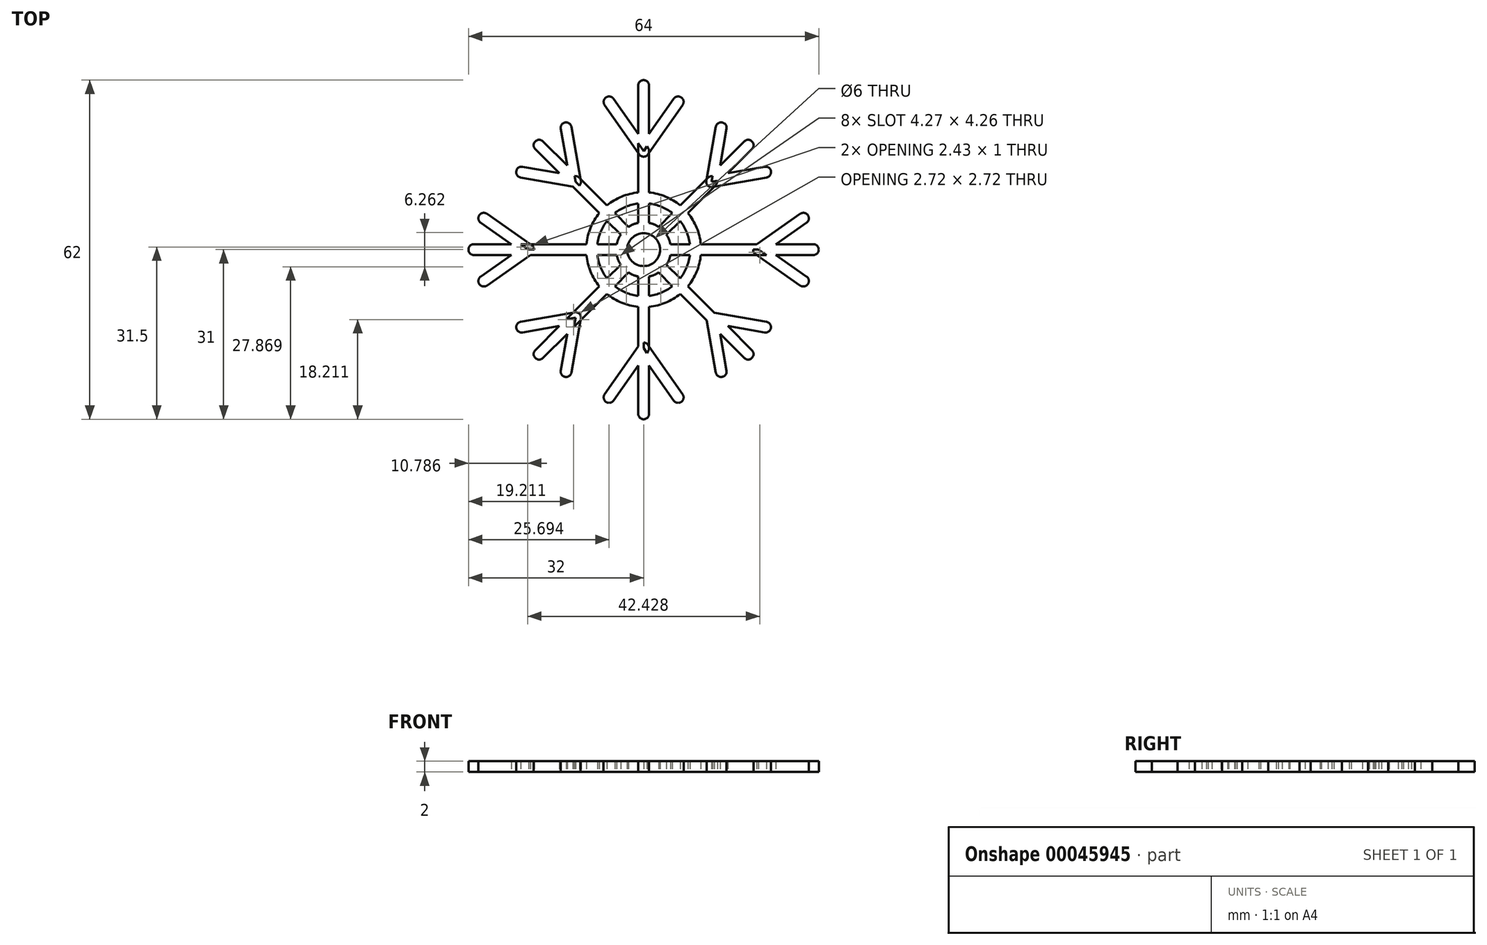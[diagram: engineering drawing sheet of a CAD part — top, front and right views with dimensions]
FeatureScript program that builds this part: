
annotation { "Feature Type Name" : "Feature", "Feature Type Description" : "" }
export const myFeature = defineFeature(function(context is Context, id is Id, definition is map)
    precondition{}
    {
        {
            var Q0;
            Q0=qCreatedBy(makeId("Top.planeOp"),FACE);
            var sketch = newSketch(context, id + "F0", { "sketchPlane" : qUnion([Q0])});
            skLineSegment(sketch, "E0", {"start": v(0, 30) * mm, "end": v(0, -124.41) * mm, "construction": true});
            skLineSegment(sketch, "E1", {"start": v(-154.84, 0) * mm, "end": v(56.08, 0) * mm, "construction": true});
            skCircle(sketch, "E2", {"center": v(0, 0) * mm, "radius": 3 * mm});
            skCircle(sketch, "E3", {"center": v(0, 0) * mm, "radius": 5 * mm});
            skCircle(sketch, "E4", {"center": v(0, 0) * mm, "radius": 8.5 * mm});
            skCircle(sketch, "E5", {"center": v(0, 0) * mm, "radius": 10.5 * mm});
            skLineSegment(sketch, "E6", {"start": v(0, 0) * mm, "end": v(0, 30) * mm});
            skArc(sketch, "E7.0.startCap", {"start": v(1, 0) * mm, "mid": v(0, -1) * mm, "end": v(-1, 0) * mm});
            skArc(sketch, "E7.0.endCap", {"start": v(-1, 30) * mm, "mid": v(0, 31) * mm, "end": v(1, 30) * mm});
            skLineSegment(sketch, "E7.0.left", {"start": v(-1, 0) * mm, "end": v(-1, 30) * mm});
            skLineSegment(sketch, "E7.0.right", {"start": v(1, 0) * mm, "end": v(1, 30) * mm});
            skLineSegment(sketch, "E8", {"start": v(1, 0) * mm, "end": v(31, 0) * mm});
            skArc(sketch, "E9.0.startCap", {"start": v(1, -1) * mm, "mid": v(0, 0) * mm, "end": v(1, 1) * mm});
            skArc(sketch, "E9.0.endCap", {"start": v(31, 1) * mm, "mid": v(32, 0) * mm, "end": v(31, -1) * mm});
            skLineSegment(sketch, "E9.0.left", {"start": v(1, 1) * mm, "end": v(31, 1) * mm});
            skLineSegment(sketch, "E9.0.right", {"start": v(1, -1) * mm, "end": v(31, -1) * mm});
            skLineSegment(sketch, "E10", {"start": v(0, 18) * mm, "end": v(6.3, 27.01) * mm});
            skArc(sketch, "E11.0.startCap", {"start": v(0.82, 17.43) * mm, "mid": v(-0.57, 17.18) * mm, "end": v(-0.82, 18.57) * mm});
            skArc(sketch, "E11.0.endCap", {"start": v(5.5, 27.58) * mm, "mid": v(6.88, 27.83) * mm, "end": v(7.13, 26.44) * mm});
            skLineSegment(sketch, "E11.0.left", {"start": v(-0.82, 18.57) * mm, "end": v(5.5, 27.58) * mm});
            skLineSegment(sketch, "E11.0.right", {"start": v(0.82, 17.43) * mm, "end": v(7.13, 26.44) * mm});
            skLineSegment(sketch, "E12", {"start": v(0, 0) * mm, "end": v(19.1, 19.1) * mm});
            skArc(sketch, "E13.0.startCap", {"start": v(0.7, -0.7) * mm, "mid": v(-0.7, -0.7) * mm, "end": v(-0.7, 0.7) * mm});
            skArc(sketch, "E13.0.endCap", {"start": v(18.38, 19.8) * mm, "mid": v(19.8, 19.8) * mm, "end": v(19.8, 18.38) * mm});
            skLineSegment(sketch, "E13.0.left", {"start": v(-0.7, 0.7) * mm, "end": v(18.38, 19.8) * mm});
            skLineSegment(sketch, "E13.0.right", {"start": v(0.7, -0.7) * mm, "end": v(19.8, 18.38) * mm});
            skLineSegment(sketch, "E14", {"start": v(21, 0) * mm, "end": v(29.2, 5.74) * mm});
            skArc(sketch, "E15.0.startCap", {"start": v(21.57, -0.82) * mm, "mid": v(20.18, -0.57) * mm, "end": v(20.43, 0.82) * mm});
            skArc(sketch, "E15.0.endCap", {"start": v(28.62, 6.55) * mm, "mid": v(30.01, 6.3) * mm, "end": v(29.77, 4.92) * mm});
            skLineSegment(sketch, "E15.0.left", {"start": v(20.43, 0.82) * mm, "end": v(28.62, 6.55) * mm});
            skLineSegment(sketch, "E15.0.right", {"start": v(21.57, -0.82) * mm, "end": v(29.77, 4.92) * mm});
            skLineSegment(sketch, "E16", {"start": v(12.43, 12.43) * mm, "end": v(22.28, 14.17) * mm});
            skLineSegment(sketch, "E17", {"start": v(12.43, 12.43) * mm, "end": v(14.17, 22.28) * mm});
            skArc(sketch, "E18.0.startCap", {"start": v(13.42, 12.26) * mm, "mid": v(12.26, 11.45) * mm, "end": v(11.45, 12.6) * mm});
            skArc(sketch, "E18.0.endCap", {"start": v(13.18, 22.45) * mm, "mid": v(14.34, 23.26) * mm, "end": v(15.15, 22.1) * mm});
            skLineSegment(sketch, "E18.0.left", {"start": v(11.45, 12.6) * mm, "end": v(13.18, 22.45) * mm});
            skLineSegment(sketch, "E18.0.right", {"start": v(13.42, 12.26) * mm, "end": v(15.15, 22.1) * mm});
            skArc(sketch, "E18.1.startCap", {"start": v(12.6, 11.45) * mm, "mid": v(11.45, 12.26) * mm, "end": v(12.26, 13.42) * mm});
            skArc(sketch, "E18.1.endCap", {"start": v(22.1, 15.15) * mm, "mid": v(23.26, 14.34) * mm, "end": v(22.45, 13.18) * mm});
            skLineSegment(sketch, "E18.1.left", {"start": v(12.26, 13.42) * mm, "end": v(22.1, 15.15) * mm});
            skLineSegment(sketch, "E18.1.right", {"start": v(12.6, 11.45) * mm, "end": v(22.45, 13.18) * mm});
            skArc(sketch, "E19.MirrorCS", {"start": v(0.7, 0.7) * mm, "mid": v(-0.7, 0.7) * mm, "end": v(-0.7, -0.7) * mm});
            skArc(sketch, "E20.MirrorCS", {"start": v(1, 0) * mm, "mid": v(0, 1) * mm, "end": v(-1, 0) * mm});
            skArc(sketch, "E21.MirrorCS", {"start": v(1, 1) * mm, "mid": v(0, 0) * mm, "end": v(1, -1) * mm});
            skArc(sketch, "E22.MirrorCS", {"start": v(12.6, -11.45) * mm, "mid": v(11.45, -12.26) * mm, "end": v(12.26, -13.42) * mm});
            skArc(sketch, "E23.MirrorCS", {"start": v(-1, -30) * mm, "mid": v(0, -31) * mm, "end": v(1, -30) * mm});
            skArc(sketch, "E24.MirrorCS", {"start": v(13.42, -12.26) * mm, "mid": v(12.26, -11.45) * mm, "end": v(11.45, -12.6) * mm});
            skArc(sketch, "E25.MirrorCS", {"start": v(21.57, 0.82) * mm, "mid": v(20.18, 0.57) * mm, "end": v(20.43, -0.82) * mm});
            skArc(sketch, "E26.MirrorCS", {"start": v(13.18, -22.45) * mm, "mid": v(14.34, -23.26) * mm, "end": v(15.15, -22.1) * mm});
            skArc(sketch, "E27.MirrorCS", {"start": v(28.62, -6.55) * mm, "mid": v(30.01, -6.3) * mm, "end": v(29.77, -4.92) * mm});
            skArc(sketch, "E28.MirrorCS", {"start": v(5.5, -27.58) * mm, "mid": v(6.88, -27.83) * mm, "end": v(7.13, -26.44) * mm});
            skArc(sketch, "E29.MirrorCS", {"start": v(18.38, -19.8) * mm, "mid": v(19.8, -19.8) * mm, "end": v(19.8, -18.38) * mm});
            skArc(sketch, "E30.MirrorCS", {"start": v(22.1, -15.15) * mm, "mid": v(23.26, -14.34) * mm, "end": v(22.45, -13.18) * mm});
            skArc(sketch, "E31.MirrorCS", {"start": v(31, -1) * mm, "mid": v(32, 0) * mm, "end": v(31, 1) * mm});
            skArc(sketch, "E32.MirrorCS", {"start": v(0.82, -17.43) * mm, "mid": v(-0.57, -17.18) * mm, "end": v(-0.82, -18.57) * mm});
            skLineSegment(sketch, "E33.MirrorCS", {"start": v(11.45, -12.6) * mm, "end": v(13.18, -22.45) * mm});
            skLineSegment(sketch, "E34.MirrorCS", {"start": v(21, 0) * mm, "end": v(29.2, -5.74) * mm});
            skLineSegment(sketch, "E35.MirrorCS", {"start": v(-0.82, -18.57) * mm, "end": v(5.5, -27.58) * mm});
            skLineSegment(sketch, "E36.MirrorCS", {"start": v(0.82, -17.43) * mm, "end": v(7.13, -26.44) * mm});
            skLineSegment(sketch, "E37.MirrorCS", {"start": v(13.42, -12.26) * mm, "end": v(15.15, -22.1) * mm});
            skLineSegment(sketch, "E38.MirrorCS", {"start": v(20.43, -0.82) * mm, "end": v(28.62, -6.55) * mm});
            skLineSegment(sketch, "E39.MirrorCS", {"start": v(0, 0) * mm, "end": v(19.1, -19.1) * mm});
            skLineSegment(sketch, "E40.MirrorCS", {"start": v(21.57, 0.82) * mm, "end": v(29.77, -4.92) * mm});
            skLineSegment(sketch, "E41.MirrorCS", {"start": v(0, 0) * mm, "end": v(0, -30) * mm});
            skLineSegment(sketch, "E42.MirrorCS", {"start": v(-1, 0) * mm, "end": v(-1, -30) * mm});
            skLineSegment(sketch, "E43.MirrorCS", {"start": v(1, 0) * mm, "end": v(1, -30) * mm});
            skLineSegment(sketch, "E44.MirrorCS", {"start": v(0.7, 0.7) * mm, "end": v(19.8, -18.38) * mm});
            skLineSegment(sketch, "E45.MirrorCS", {"start": v(12.26, -13.42) * mm, "end": v(22.1, -15.15) * mm});
            skLineSegment(sketch, "E46.MirrorCS", {"start": v(0, -18) * mm, "end": v(6.3, -27.01) * mm});
            skLineSegment(sketch, "E47.MirrorCS", {"start": v(12.43, -12.43) * mm, "end": v(14.17, -22.28) * mm});
            skLineSegment(sketch, "E48.MirrorCS", {"start": v(12.43, -12.43) * mm, "end": v(22.28, -14.17) * mm});
            skLineSegment(sketch, "E49.MirrorCS", {"start": v(12.6, -11.45) * mm, "end": v(22.45, -13.18) * mm});
            skLineSegment(sketch, "E50.MirrorCS", {"start": v(-0.7, -0.7) * mm, "end": v(18.38, -19.8) * mm});
            skArc(sketch, "E51.MirrorCS", {"start": v(-0.7, -0.7) * mm, "mid": v(0.7, -0.7) * mm, "end": v(0.7, 0.7) * mm});
            skArc(sketch, "E52.MirrorCS", {"start": v(-1, 1) * mm, "mid": v(0, 0) * mm, "end": v(-1, -1) * mm});
            skArc(sketch, "E53.MirrorCS", {"start": v(-0.7, 0.7) * mm, "mid": v(0.7, 0.7) * mm, "end": v(0.7, -0.7) * mm});
            skArc(sketch, "E54.MirrorCS", {"start": v(-1, -1) * mm, "mid": v(0, 0) * mm, "end": v(-1, 1) * mm});
            skArc(sketch, "E55.MirrorCS", {"start": v(-1, 0) * mm, "mid": v(0, -1) * mm, "end": v(1, 0) * mm});
            skArc(sketch, "E56.MirrorCS", {"start": v(-1, 0) * mm, "mid": v(0, 1) * mm, "end": v(1, 0) * mm});
            skArc(sketch, "E57.MirrorCS", {"start": v(-13.42, -12.26) * mm, "mid": v(-12.26, -11.45) * mm, "end": v(-11.45, -12.6) * mm});
            skArc(sketch, "E58.MirrorCS", {"start": v(-12.6, -11.45) * mm, "mid": v(-11.45, -12.26) * mm, "end": v(-12.26, -13.42) * mm});
            skArc(sketch, "E59.MirrorCS", {"start": v(-31, -1) * mm, "mid": v(-32, 0) * mm, "end": v(-31, 1) * mm});
            skArc(sketch, "E60.MirrorCS", {"start": v(-13.42, 12.26) * mm, "mid": v(-12.26, 11.45) * mm, "end": v(-11.45, 12.6) * mm});
            skArc(sketch, "E61.MirrorCS", {"start": v(-31, 1) * mm, "mid": v(-32, 0) * mm, "end": v(-31, -1) * mm});
            skArc(sketch, "E62.MirrorCS", {"start": v(-12.6, 11.45) * mm, "mid": v(-11.45, 12.26) * mm, "end": v(-12.26, 13.42) * mm});
            skArc(sketch, "E63.MirrorCS", {"start": v(1, 30) * mm, "mid": v(0, 31) * mm, "end": v(-1, 30) * mm});
            skArc(sketch, "E64.MirrorCS", {"start": v(-21.57, 0.82) * mm, "mid": v(-20.18, 0.57) * mm, "end": v(-20.43, -0.82) * mm});
            skArc(sketch, "E65.MirrorCS", {"start": v(-21.57, -0.82) * mm, "mid": v(-20.18, -0.57) * mm, "end": v(-20.43, 0.82) * mm});
            skArc(sketch, "E66.MirrorCS", {"start": v(-13.18, 22.45) * mm, "mid": v(-14.34, 23.26) * mm, "end": v(-15.15, 22.1) * mm});
            skArc(sketch, "E67.MirrorCS", {"start": v(-13.18, -22.45) * mm, "mid": v(-14.34, -23.26) * mm, "end": v(-15.15, -22.1) * mm});
            skArc(sketch, "E68.MirrorCS", {"start": v(1, -30) * mm, "mid": v(0, -31) * mm, "end": v(-1, -30) * mm});
            skArc(sketch, "E69.MirrorCS", {"start": v(-22.1, -15.15) * mm, "mid": v(-23.26, -14.34) * mm, "end": v(-22.45, -13.18) * mm});
            skArc(sketch, "E70.MirrorCS", {"start": v(-5.5, -27.58) * mm, "mid": v(-6.88, -27.83) * mm, "end": v(-7.13, -26.44) * mm});
            skArc(sketch, "E71.MirrorCS", {"start": v(-5.5, 27.58) * mm, "mid": v(-6.88, 27.83) * mm, "end": v(-7.13, 26.44) * mm});
            skArc(sketch, "E72.MirrorCS", {"start": v(-28.62, -6.55) * mm, "mid": v(-30.01, -6.3) * mm, "end": v(-29.77, -4.92) * mm});
            skArc(sketch, "E73.MirrorCS", {"start": v(-0.82, 17.43) * mm, "mid": v(0.57, 17.18) * mm, "end": v(0.82, 18.57) * mm});
            skArc(sketch, "E74.MirrorCS", {"start": v(-28.62, 6.55) * mm, "mid": v(-30.01, 6.3) * mm, "end": v(-29.77, 4.92) * mm});
            skArc(sketch, "E75.MirrorCS", {"start": v(-18.38, 19.8) * mm, "mid": v(-19.8, 19.8) * mm, "end": v(-19.8, 18.38) * mm});
            skArc(sketch, "E76.MirrorCS", {"start": v(-22.1, 15.15) * mm, "mid": v(-23.26, 14.34) * mm, "end": v(-22.45, 13.18) * mm});
            skArc(sketch, "E77.MirrorCS", {"start": v(-0.82, -17.43) * mm, "mid": v(0.57, -17.18) * mm, "end": v(0.82, -18.57) * mm});
            skArc(sketch, "E78.MirrorCS", {"start": v(-18.38, -19.8) * mm, "mid": v(-19.8, -19.8) * mm, "end": v(-19.8, -18.38) * mm});
            skLineSegment(sketch, "E79.MirrorCS", {"start": v(-1, 0) * mm, "end": v(-31, 0) * mm});
            skLineSegment(sketch, "E80.MirrorCS", {"start": v(-1, 1) * mm, "end": v(-31, 1) * mm});
            skLineSegment(sketch, "E81.MirrorCS", {"start": v(-1, -1) * mm, "end": v(-31, -1) * mm});
            skLineSegment(sketch, "E82.MirrorCS", {"start": v(-11.45, 12.6) * mm, "end": v(-13.18, 22.45) * mm});
            skLineSegment(sketch, "E83.MirrorCS", {"start": v(-12.43, 12.43) * mm, "end": v(-14.17, 22.28) * mm});
            skLineSegment(sketch, "E84.MirrorCS", {"start": v(0, 18) * mm, "end": v(-6.3, 27.01) * mm});
            skLineSegment(sketch, "E85.MirrorCS", {"start": v(-12.43, 12.43) * mm, "end": v(-22.28, 14.17) * mm});
            skLineSegment(sketch, "E86.MirrorCS", {"start": v(-21.57, -0.82) * mm, "end": v(-29.77, 4.92) * mm});
            skLineSegment(sketch, "E87.MirrorCS", {"start": v(-21.57, 0.82) * mm, "end": v(-29.77, -4.92) * mm});
            skLineSegment(sketch, "E88.MirrorCS", {"start": v(-20.43, -0.82) * mm, "end": v(-28.62, -6.55) * mm});
            skLineSegment(sketch, "E89.MirrorCS", {"start": v(-20.43, 0.82) * mm, "end": v(-28.62, 6.55) * mm});
            skLineSegment(sketch, "E90.MirrorCS", {"start": v(0, 0) * mm, "end": v(-19.1, -19.1) * mm});
            skLineSegment(sketch, "E91.MirrorCS", {"start": v(-12.6, -11.45) * mm, "end": v(-22.45, -13.18) * mm});
            skLineSegment(sketch, "E92.MirrorCS", {"start": v(0.7, 0.7) * mm, "end": v(-18.38, 19.8) * mm});
            skLineSegment(sketch, "E93.MirrorCS", {"start": v(-12.6, 11.45) * mm, "end": v(-22.45, 13.18) * mm});
            skLineSegment(sketch, "E94.MirrorCS", {"start": v(-13.42, -12.26) * mm, "end": v(-15.15, -22.1) * mm});
            skLineSegment(sketch, "E95.MirrorCS", {"start": v(-21, 0) * mm, "end": v(-29.2, -5.74) * mm});
            skLineSegment(sketch, "E96.MirrorCS", {"start": v(-12.43, -12.43) * mm, "end": v(-22.28, -14.17) * mm});
            skLineSegment(sketch, "E97.MirrorCS", {"start": v(-12.26, 13.42) * mm, "end": v(-22.1, 15.15) * mm});
            skLineSegment(sketch, "E98.MirrorCS", {"start": v(-11.45, -12.6) * mm, "end": v(-13.18, -22.45) * mm});
            skLineSegment(sketch, "E99.MirrorCS", {"start": v(-21, 0) * mm, "end": v(-29.2, 5.74) * mm});
            skLineSegment(sketch, "E100.MirrorCS", {"start": v(-12.43, -12.43) * mm, "end": v(-14.17, -22.28) * mm});
            skLineSegment(sketch, "E101.MirrorCS", {"start": v(-0.82, -17.43) * mm, "end": v(-7.13, -26.44) * mm});
            skLineSegment(sketch, "E102.MirrorCS", {"start": v(-13.42, 12.26) * mm, "end": v(-15.15, 22.1) * mm});
            skLineSegment(sketch, "E103.MirrorCS", {"start": v(-12.26, -13.42) * mm, "end": v(-22.1, -15.15) * mm});
            skLineSegment(sketch, "E104.MirrorCS", {"start": v(-0.82, 17.43) * mm, "end": v(-7.13, 26.44) * mm});
            skLineSegment(sketch, "E105.MirrorCS", {"start": v(0.82, 18.57) * mm, "end": v(-5.5, 27.58) * mm});
            skLineSegment(sketch, "E106.MirrorCS", {"start": v(0, 0) * mm, "end": v(-19.1, 19.1) * mm});
            skLineSegment(sketch, "E107.MirrorCS", {"start": v(-0.7, -0.7) * mm, "end": v(-19.8, 18.38) * mm});
            skLineSegment(sketch, "E108.MirrorCS", {"start": v(0.7, -0.7) * mm, "end": v(-18.38, -19.8) * mm});
            skLineSegment(sketch, "E109.MirrorCS", {"start": v(0.82, -18.57) * mm, "end": v(-5.5, -27.58) * mm});
            skLineSegment(sketch, "E110.MirrorCS", {"start": v(-0.7, 0.7) * mm, "end": v(-19.8, -18.38) * mm});
            skLineSegment(sketch, "E111.MirrorCS", {"start": v(0, -18) * mm, "end": v(-6.3, -27.01) * mm});
            skSolve(sketch);
        }
        {
            var Q0;
            Q0 = qSketchRegion(id + "F0", true);
            var Q1;
            {var subQ1=sQuery(id+"F0.wireOp",EDGE,"E62.MirrorCS");var subQ8=makeQuery(id+"F0.imprint","INTERSECT",VERTEX,{"derivedFrom":[subQ1,sQuery(id+"F0.wireOp",EDGE,"E82.MirrorCS")]});Q1=makeQuery(id+"F0.imprint","IMPRINT",FACE,{"disambiguationData":[TD([[makeQuery(id+"F0.imprint","IMPRINT",EDGE,{"disambiguationData":[TD([[subQ8,1.0]])],"derivedFrom":subQ1}),1.0]])]});}
            var Q2;
            {var subQ1=sQuery(id+"F0.wireOp",EDGE,"E97.MirrorCS");var subQ3=sQuery(id+"F0.wireOp",EDGE,"E83.MirrorCS");var subQ5=makeQuery(id+"F0.imprint","INTERSECT",VERTEX,{"derivedFrom":[subQ3,subQ1]});Q2=makeQuery(id+"F0.imprint","IMPRINT",FACE,{"disambiguationData":[TD([[makeQuery(id+"F0.imprint","IMPRINT",EDGE,{"disambiguationData":[TD([[subQ5,1.0]])],"derivedFrom":subQ3}),1.0]])]});}
            var Q3;
            {var subQ1=sQuery(id+"F0.wireOp",EDGE,"E97.MirrorCS");var subQ5=sQuery(id+"F0.wireOp",EDGE,"E62.MirrorCS");var subQ6=makeQuery(id+"F0.imprint","INTERSECT",VERTEX,{"derivedFrom":[subQ5,subQ1]});Q3=makeQuery(id+"F0.imprint","IMPRINT",FACE,{"disambiguationData":[TD([[makeQuery(id+"F0.imprint","IMPRINT",EDGE,{"disambiguationData":[TD([[subQ6,1.0]])],"derivedFrom":subQ5}),-1.0]])]});}
            var Q4;
            {var subQ1=sQuery(id+"F0.wireOp",EDGE,"E102.MirrorCS");var subQ3=sQuery(id+"F0.wireOp",EDGE,"E85.MirrorCS");var subQ5=makeQuery(id+"F0.imprint","INTERSECT",VERTEX,{"derivedFrom":[subQ3,subQ1]});Q4=makeQuery(id+"F0.imprint","IMPRINT",FACE,{"disambiguationData":[TD([[makeQuery(id+"F0.imprint","IMPRINT",EDGE,{"disambiguationData":[TD([[subQ5,1.0]])],"derivedFrom":subQ3}),-1.0]])]});}
            var Q5;
            {var subQ1=sQuery(id+"F0.wireOp",EDGE,"E60.MirrorCS");var subQ5=sQuery(id+"F0.wireOp",EDGE,"E102.MirrorCS");var subQ7=makeQuery(id+"F0.imprint","INTERSECT",VERTEX,{"derivedFrom":[subQ1,subQ5]});Q5=makeQuery(id+"F0.imprint","IMPRINT",FACE,{"disambiguationData":[TD([[makeQuery(id+"F0.imprint","IMPRINT",EDGE,{"disambiguationData":[TD([[subQ7,-1.0]])],"derivedFrom":subQ1}),-1.0]])]});}
            var Q6;
            {var subQ5=sQuery(id+"F0.wireOp",EDGE,"E102.MirrorCS");var subQ7=sQuery(id+"F0.wireOp",EDGE,"E60.MirrorCS");var subQ8=makeQuery(id+"F0.imprint","INTERSECT",VERTEX,{"derivedFrom":[subQ7,subQ5]});Q6=makeQuery(id+"F0.imprint","IMPRINT",FACE,{"disambiguationData":[TD([[makeQuery(id+"F0.imprint","IMPRINT",EDGE,{"disambiguationData":[TD([[subQ8,-1.0]])],"derivedFrom":subQ7}),1.0]])]});}
            var Q7;
            {var subQ5=sQuery(id+"F0.wireOp",EDGE,"E11.0.left");var subQ7=sQuery(id+"F0.wireOp",EDGE,"E11.0.startCap");var subQ10=makeQuery(id+"F0.imprint","INTERSECT",VERTEX,{"derivedFrom":[subQ7,subQ5]});Q7=makeQuery(id+"F0.imprint","IMPRINT",FACE,{"disambiguationData":[TD([[makeQuery(id+"F0.imprint","IMPRINT",EDGE,{"disambiguationData":[TD([[subQ10,1.0]])],"derivedFrom":subQ7}),-1.0]])]});}
            var Q8;
            {var subQ1=sQuery(id+"F0.wireOp",EDGE,"E11.0.startCap");var subQ5=sQuery(id+"F0.wireOp",EDGE,"E11.0.left");var subQ7=makeQuery(id+"F0.imprint","INTERSECT",VERTEX,{"derivedFrom":[subQ1,subQ5]});Q8=makeQuery(id+"F0.imprint","IMPRINT",FACE,{"disambiguationData":[TD([[makeQuery(id+"F0.imprint","IMPRINT",EDGE,{"disambiguationData":[TD([[subQ7,1.0]])],"derivedFrom":subQ1}),1.0]])]});}
            var Q9;
            {var subQ0=sQuery(id+"F0.wireOp",EDGE,"E84.MirrorCS");var subQ1=sQuery(id+"F0.wireOp",EDGE,"E11.0.left");var subQ2=makeQuery(id+"F0.imprint","INTERSECT",VERTEX,{"derivedFrom":[subQ1,subQ0]});Q9=makeQuery(id+"F0.imprint","IMPRINT",FACE,{"disambiguationData":[TD([[makeQuery(id+"F0.imprint","IMPRINT",EDGE,{"disambiguationData":[TD([[subQ2,-1.0]])],"derivedFrom":subQ1}),-1.0]])]});}
            var Q10;
            {var subQ0=sQuery(id+"F0.wireOp",EDGE,"E105.MirrorCS");var subQ3=sQuery(id+"F0.wireOp",EDGE,"E10");var subQ4=makeQuery(id+"F0.imprint","INTERSECT",VERTEX,{"derivedFrom":[subQ3,subQ0]});Q10=makeQuery(id+"F0.imprint","IMPRINT",FACE,{"disambiguationData":[TD([[makeQuery(id+"F0.imprint","IMPRINT",EDGE,{"disambiguationData":[TD([[subQ4,1.0]])],"derivedFrom":subQ3}),1.0]])]});}
            var Q11;
            {var subQ3=sQuery(id+"F0.wireOp",EDGE,"E73.MirrorCS");var subQ8=makeQuery(id+"F0.imprint","INTERSECT",VERTEX,{"derivedFrom":[sQuery(id+"F0.wireOp",EDGE,"E11.0.right"),subQ3]});Q11=makeQuery(id+"F0.imprint","IMPRINT",FACE,{"disambiguationData":[TD([[makeQuery(id+"F0.imprint","IMPRINT",EDGE,{"disambiguationData":[TD([[subQ8,1.0]])],"derivedFrom":subQ3}),1.0]])]});}
            var Q12;
            {var subQ1=sQuery(id+"F0.wireOp",EDGE,"E7.0.right");var subQ5=sQuery(id+"F0.wireOp",EDGE,"E10");var subQ7=makeQuery(id+"F0.imprint","INTERSECT",VERTEX,{"derivedFrom":[subQ5,subQ1]});Q12=makeQuery(id+"F0.imprint","IMPRINT",FACE,{"disambiguationData":[TD([[makeQuery(id+"F0.imprint","IMPRINT",EDGE,{"disambiguationData":[TD([[subQ7,1.0]])],"derivedFrom":subQ5}),-1.0]])]});}
            var Q13;
            {var subQ0=sQuery(id+"F0.wireOp",EDGE,"E18.1.left");var subQ3=sQuery(id+"F0.wireOp",EDGE,"E17");var subQ4=makeQuery(id+"F0.imprint","INTERSECT",VERTEX,{"derivedFrom":[subQ3,subQ0]});Q13=makeQuery(id+"F0.imprint","IMPRINT",FACE,{"disambiguationData":[TD([[makeQuery(id+"F0.imprint","IMPRINT",EDGE,{"disambiguationData":[TD([[subQ4,1.0]])],"derivedFrom":subQ3}),-1.0]])]});}
            var Q14;
            {var subQ0=sQuery(id+"F0.wireOp",EDGE,"E16");var subQ1=sQuery(id+"F0.wireOp",EDGE,"E18.0.right");var subQ2=makeQuery(id+"F0.imprint","INTERSECT",VERTEX,{"derivedFrom":[subQ0,subQ1]});Q14=makeQuery(id+"F0.imprint","IMPRINT",FACE,{"disambiguationData":[TD([[makeQuery(id+"F0.imprint","IMPRINT",EDGE,{"disambiguationData":[TD([[subQ2,1.0]])],"derivedFrom":subQ0}),1.0]])]});}
            var Q15;
            {var subQ0=sQuery(id+"F0.wireOp",EDGE,"E18.1.startCap");var subQ9=makeQuery(id+"F0.imprint","INTERSECT",VERTEX,{"derivedFrom":[sQuery(id+"F0.wireOp",EDGE,"E18.0.left"),subQ0]});Q15=makeQuery(id+"F0.imprint","IMPRINT",FACE,{"disambiguationData":[TD([[makeQuery(id+"F0.imprint","IMPRINT",EDGE,{"disambiguationData":[TD([[subQ9,1.0]])],"derivedFrom":subQ0}),-1.0]])]});}
            var Q16;
            {var subQ1=sQuery(id+"F0.wireOp",EDGE,"E17");var subQ5=sQuery(id+"F0.wireOp",EDGE,"E13.0.left");var subQ7=makeQuery(id+"F0.imprint","INTERSECT",VERTEX,{"derivedFrom":[subQ5,subQ1]});Q16=makeQuery(id+"F0.imprint","IMPRINT",FACE,{"disambiguationData":[TD([[makeQuery(id+"F0.imprint","IMPRINT",EDGE,{"disambiguationData":[TD([[subQ7,1.0]])],"derivedFrom":subQ5}),-1.0]])]});}
            var Q17;
            {var subQ5=sQuery(id+"F0.wireOp",EDGE,"E18.0.startCap");var subQ7=sQuery(id+"F0.wireOp",EDGE,"E18.0.right");var subQ10=makeQuery(id+"F0.imprint","INTERSECT",VERTEX,{"derivedFrom":[subQ5,subQ7]});Q17=makeQuery(id+"F0.imprint","IMPRINT",FACE,{"disambiguationData":[TD([[makeQuery(id+"F0.imprint","IMPRINT",EDGE,{"disambiguationData":[TD([[subQ10,-1.0]])],"derivedFrom":subQ5}),-1.0]])]});}
            var Q18;
            {var subQ1=sQuery(id+"F0.wireOp",EDGE,"E16");var subQ5=sQuery(id+"F0.wireOp",EDGE,"E13.0.right");var subQ7=makeQuery(id+"F0.imprint","INTERSECT",VERTEX,{"derivedFrom":[subQ5,subQ1]});Q18=makeQuery(id+"F0.imprint","IMPRINT",FACE,{"disambiguationData":[TD([[makeQuery(id+"F0.imprint","IMPRINT",EDGE,{"disambiguationData":[TD([[subQ7,1.0]])],"derivedFrom":subQ5}),1.0]])]});}
            var Q19;
            {var subQ0=sQuery(id+"F0.wireOp",EDGE,"E9.0.left");var subQ3=sQuery(id+"F0.wireOp",EDGE,"E14");var subQ4=makeQuery(id+"F0.imprint","INTERSECT",VERTEX,{"derivedFrom":[subQ3,subQ0]});Q19=makeQuery(id+"F0.imprint","IMPRINT",FACE,{"disambiguationData":[TD([[makeQuery(id+"F0.imprint","IMPRINT",EDGE,{"disambiguationData":[TD([[subQ4,1.0]])],"derivedFrom":subQ3}),1.0]])]});}
            var Q20;
            {var subQ1=sQuery(id+"F0.wireOp",EDGE,"E25.MirrorCS");var subQ5=sQuery(id+"F0.wireOp",EDGE,"E40.MirrorCS");var subQ7=makeQuery(id+"F0.imprint","INTERSECT",VERTEX,{"derivedFrom":[subQ1,subQ5]});Q20=makeQuery(id+"F0.imprint","IMPRINT",FACE,{"disambiguationData":[TD([[makeQuery(id+"F0.imprint","IMPRINT",EDGE,{"disambiguationData":[TD([[subQ7,-1.0]])],"derivedFrom":subQ1}),1.0]])]});}
            var Q21;
            {var subQ1=sQuery(id+"F0.wireOp",EDGE,"E40.MirrorCS");var subQ3=sQuery(id+"F0.wireOp",EDGE,"E14");var subQ5=makeQuery(id+"F0.imprint","INTERSECT",VERTEX,{"derivedFrom":[subQ3,subQ1]});Q21=makeQuery(id+"F0.imprint","IMPRINT",FACE,{"disambiguationData":[TD([[makeQuery(id+"F0.imprint","IMPRINT",EDGE,{"disambiguationData":[TD([[subQ5,1.0]])],"derivedFrom":subQ3}),-1.0]])]});}
            var Q22;
            {var subQ5=sQuery(id+"F0.wireOp",EDGE,"E15.0.right");var subQ7=sQuery(id+"F0.wireOp",EDGE,"E15.0.startCap");var subQ9=makeQuery(id+"F0.imprint","INTERSECT",VERTEX,{"derivedFrom":[subQ7,subQ5]});Q22=makeQuery(id+"F0.imprint","IMPRINT",FACE,{"disambiguationData":[TD([[makeQuery(id+"F0.imprint","IMPRINT",EDGE,{"disambiguationData":[TD([[subQ9,-1.0]])],"derivedFrom":subQ7}),-1.0]])]});}
            var Q23;
            {var subQ1=sQuery(id+"F0.wireOp",EDGE,"E15.0.right");var subQ3=sQuery(id+"F0.wireOp",EDGE,"E34.MirrorCS");var subQ5=makeQuery(id+"F0.imprint","INTERSECT",VERTEX,{"derivedFrom":[subQ1,subQ3]});Q23=makeQuery(id+"F0.imprint","IMPRINT",FACE,{"disambiguationData":[TD([[makeQuery(id+"F0.imprint","IMPRINT",EDGE,{"disambiguationData":[TD([[subQ5,-1.0]])],"derivedFrom":subQ1}),1.0]])]});}
            var Q24;
            {var subQ1=sQuery(id+"F0.wireOp",EDGE,"E15.0.startCap");var subQ5=sQuery(id+"F0.wireOp",EDGE,"E15.0.right");var subQ7=makeQuery(id+"F0.imprint","INTERSECT",VERTEX,{"derivedFrom":[subQ1,subQ5]});Q24=makeQuery(id+"F0.imprint","IMPRINT",FACE,{"disambiguationData":[TD([[makeQuery(id+"F0.imprint","IMPRINT",EDGE,{"disambiguationData":[TD([[subQ7,-1.0]])],"derivedFrom":subQ1}),1.0]])]});}
            var Q25;
            {var subQ1=sQuery(id+"F0.wireOp",EDGE,"E37.MirrorCS");var subQ5=sQuery(id+"F0.wireOp",EDGE,"E24.MirrorCS");var subQ7=makeQuery(id+"F0.imprint","INTERSECT",VERTEX,{"derivedFrom":[subQ5,subQ1]});Q25=makeQuery(id+"F0.imprint","IMPRINT",FACE,{"disambiguationData":[TD([[makeQuery(id+"F0.imprint","IMPRINT",EDGE,{"disambiguationData":[TD([[subQ7,-1.0]])],"derivedFrom":subQ5}),1.0]])]});}
            var Q26;
            {var subQ1=sQuery(id+"F0.wireOp",EDGE,"E45.MirrorCS");var subQ5=sQuery(id+"F0.wireOp",EDGE,"E22.MirrorCS");var subQ9=makeQuery(id+"F0.imprint","INTERSECT",VERTEX,{"derivedFrom":[subQ5,subQ1]});Q26=makeQuery(id+"F0.imprint","IMPRINT",FACE,{"disambiguationData":[TD([[makeQuery(id+"F0.imprint","IMPRINT",EDGE,{"disambiguationData":[TD([[subQ9,1.0]])],"derivedFrom":subQ5}),1.0]])]});}
            var Q27;
            {var subQ1=sQuery(id+"F0.wireOp",EDGE,"E22.MirrorCS");var subQ5=sQuery(id+"F0.wireOp",EDGE,"E45.MirrorCS");var subQ7=makeQuery(id+"F0.imprint","INTERSECT",VERTEX,{"derivedFrom":[subQ1,subQ5]});Q27=makeQuery(id+"F0.imprint","IMPRINT",FACE,{"disambiguationData":[TD([[makeQuery(id+"F0.imprint","IMPRINT",EDGE,{"disambiguationData":[TD([[subQ7,1.0]])],"derivedFrom":subQ1}),-1.0]])]});}
            var Q28;
            {var subQ0=sQuery(id+"F0.wireOp",EDGE,"E47.MirrorCS");var subQ1=sQuery(id+"F0.wireOp",EDGE,"E45.MirrorCS");var subQ2=makeQuery(id+"F0.imprint","INTERSECT",VERTEX,{"derivedFrom":[subQ1,subQ0]});Q28=makeQuery(id+"F0.imprint","IMPRINT",FACE,{"disambiguationData":[TD([[makeQuery(id+"F0.imprint","IMPRINT",EDGE,{"disambiguationData":[TD([[subQ2,-1.0]])],"derivedFrom":subQ1}),1.0]])]});}
            var Q29;
            {var subQ0=sQuery(id+"F0.wireOp",EDGE,"E48.MirrorCS");var subQ1=sQuery(id+"F0.wireOp",EDGE,"E37.MirrorCS");var subQ2=makeQuery(id+"F0.imprint","INTERSECT",VERTEX,{"derivedFrom":[subQ1,subQ0]});Q29=makeQuery(id+"F0.imprint","IMPRINT",FACE,{"disambiguationData":[TD([[makeQuery(id+"F0.imprint","IMPRINT",EDGE,{"disambiguationData":[TD([[subQ2,-1.0]])],"derivedFrom":subQ1}),-1.0]])]});}
            var Q30;
            {var subQ1=sQuery(id+"F0.wireOp",EDGE,"E37.MirrorCS");var subQ5=sQuery(id+"F0.wireOp",EDGE,"E24.MirrorCS");var subQ7=makeQuery(id+"F0.imprint","INTERSECT",VERTEX,{"derivedFrom":[subQ5,subQ1]});Q30=makeQuery(id+"F0.imprint","IMPRINT",FACE,{"disambiguationData":[TD([[makeQuery(id+"F0.imprint","IMPRINT",EDGE,{"disambiguationData":[TD([[subQ7,-1.0]])],"derivedFrom":subQ5}),-1.0]])]});}
            var Q31;
            {var subQ3=sQuery(id+"F0.wireOp",EDGE,"E77.MirrorCS");var subQ8=makeQuery(id+"F0.imprint","INTERSECT",VERTEX,{"derivedFrom":[sQuery(id+"F0.wireOp",EDGE,"E36.MirrorCS"),subQ3]});Q31=makeQuery(id+"F0.imprint","IMPRINT",FACE,{"disambiguationData":[TD([[makeQuery(id+"F0.imprint","IMPRINT",EDGE,{"disambiguationData":[TD([[subQ8,1.0]])],"derivedFrom":subQ3}),-1.0]])]});}
            var Q32;
            {var subQ1=sQuery(id+"F0.wireOp",EDGE,"E35.MirrorCS");var subQ7=sQuery(id+"F0.wireOp",EDGE,"E32.MirrorCS");var subQ9=makeQuery(id+"F0.imprint","INTERSECT",VERTEX,{"derivedFrom":[subQ7,subQ1]});Q32=makeQuery(id+"F0.imprint","IMPRINT",FACE,{"disambiguationData":[TD([[makeQuery(id+"F0.imprint","IMPRINT",EDGE,{"disambiguationData":[TD([[subQ9,1.0]])],"derivedFrom":subQ7}),1.0]])]});}
            var Q33;
            {var subQ1=sQuery(id+"F0.wireOp",EDGE,"E35.MirrorCS");var subQ5=sQuery(id+"F0.wireOp",EDGE,"E32.MirrorCS");var subQ7=makeQuery(id+"F0.imprint","INTERSECT",VERTEX,{"derivedFrom":[subQ5,subQ1]});Q33=makeQuery(id+"F0.imprint","IMPRINT",FACE,{"disambiguationData":[TD([[makeQuery(id+"F0.imprint","IMPRINT",EDGE,{"disambiguationData":[TD([[subQ7,1.0]])],"derivedFrom":subQ5}),-1.0]])]});}
            var Q34;
            {var subQ0=sQuery(id+"F0.wireOp",EDGE,"E111.MirrorCS");var subQ1=sQuery(id+"F0.wireOp",EDGE,"E35.MirrorCS");var subQ2=makeQuery(id+"F0.imprint","INTERSECT",VERTEX,{"derivedFrom":[subQ1,subQ0]});Q34=makeQuery(id+"F0.imprint","IMPRINT",FACE,{"disambiguationData":[TD([[makeQuery(id+"F0.imprint","IMPRINT",EDGE,{"disambiguationData":[TD([[subQ2,-1.0]])],"derivedFrom":subQ1}),1.0]])]});}
            var Q35;
            {var subQ0=sQuery(id+"F0.wireOp",EDGE,"E109.MirrorCS");var subQ3=sQuery(id+"F0.wireOp",EDGE,"E46.MirrorCS");var subQ4=makeQuery(id+"F0.imprint","INTERSECT",VERTEX,{"derivedFrom":[subQ3,subQ0]});Q35=makeQuery(id+"F0.imprint","IMPRINT",FACE,{"disambiguationData":[TD([[makeQuery(id+"F0.imprint","IMPRINT",EDGE,{"disambiguationData":[TD([[subQ4,1.0]])],"derivedFrom":subQ3}),-1.0]])]});}
            var Q36;
            {var subQ1=sQuery(id+"F0.wireOp",EDGE,"E46.MirrorCS");var subQ5=sQuery(id+"F0.wireOp",EDGE,"E43.MirrorCS");var subQ7=makeQuery(id+"F0.imprint","INTERSECT",VERTEX,{"derivedFrom":[subQ1,subQ5]});Q36=makeQuery(id+"F0.imprint","IMPRINT",FACE,{"disambiguationData":[TD([[makeQuery(id+"F0.imprint","IMPRINT",EDGE,{"disambiguationData":[TD([[subQ7,1.0]])],"derivedFrom":subQ1}),1.0]])]});}
            var Q37;
            {var subQ1=sQuery(id+"F0.wireOp",EDGE,"E94.MirrorCS");var subQ5=sQuery(id+"F0.wireOp",EDGE,"E57.MirrorCS");var subQ6=makeQuery(id+"F0.imprint","INTERSECT",VERTEX,{"derivedFrom":[subQ5,subQ1]});Q37=makeQuery(id+"F0.imprint","IMPRINT",FACE,{"disambiguationData":[TD([[makeQuery(id+"F0.imprint","IMPRINT",EDGE,{"disambiguationData":[TD([[subQ6,-1.0]])],"derivedFrom":subQ5}),-1.0]])]});}
            var Q38;
            {var subQ1=sQuery(id+"F0.wireOp",EDGE,"E94.MirrorCS");var subQ5=sQuery(id+"F0.wireOp",EDGE,"E57.MirrorCS");var subQ7=makeQuery(id+"F0.imprint","INTERSECT",VERTEX,{"derivedFrom":[subQ5,subQ1]});Q38=makeQuery(id+"F0.imprint","IMPRINT",FACE,{"disambiguationData":[TD([[makeQuery(id+"F0.imprint","IMPRINT",EDGE,{"disambiguationData":[TD([[subQ7,-1.0]])],"derivedFrom":subQ5}),1.0]])]});}
            var Q39;
            {var subQ0=sQuery(id+"F0.wireOp",EDGE,"E94.MirrorCS");var subQ3=sQuery(id+"F0.wireOp",EDGE,"E96.MirrorCS");var subQ4=makeQuery(id+"F0.imprint","INTERSECT",VERTEX,{"derivedFrom":[subQ0,subQ3]});Q39=makeQuery(id+"F0.imprint","IMPRINT",FACE,{"disambiguationData":[TD([[makeQuery(id+"F0.imprint","IMPRINT",EDGE,{"disambiguationData":[TD([[subQ4,-1.0]])],"derivedFrom":subQ0}),1.0]])]});}
            var Q40;
            {var subQ0=sQuery(id+"F0.wireOp",EDGE,"E103.MirrorCS");var subQ3=sQuery(id+"F0.wireOp",EDGE,"E100.MirrorCS");var subQ4=makeQuery(id+"F0.imprint","INTERSECT",VERTEX,{"derivedFrom":[subQ3,subQ0]});Q40=makeQuery(id+"F0.imprint","IMPRINT",FACE,{"disambiguationData":[TD([[makeQuery(id+"F0.imprint","IMPRINT",EDGE,{"disambiguationData":[TD([[subQ4,1.0]])],"derivedFrom":subQ3}),-1.0]])]});}
            var Q41;
            {var subQ5=sQuery(id+"F0.wireOp",EDGE,"E58.MirrorCS");var subQ7=makeQuery(id+"F0.imprint","INTERSECT",VERTEX,{"derivedFrom":[subQ5,sQuery(id+"F0.wireOp",EDGE,"E98.MirrorCS")]});Q41=makeQuery(id+"F0.imprint","IMPRINT",FACE,{"disambiguationData":[TD([[makeQuery(id+"F0.imprint","IMPRINT",EDGE,{"disambiguationData":[TD([[subQ7,1.0]])],"derivedFrom":subQ5}),-1.0]])]});}
            var Q42;
            {var subQ0=sQuery(id+"F0.wireOp",EDGE,"E103.MirrorCS");var subQ3=sQuery(id+"F0.wireOp",EDGE,"E58.MirrorCS");var subQ4=makeQuery(id+"F0.imprint","INTERSECT",VERTEX,{"derivedFrom":[subQ3,subQ0]});Q42=makeQuery(id+"F0.imprint","IMPRINT",FACE,{"disambiguationData":[TD([[makeQuery(id+"F0.imprint","IMPRINT",EDGE,{"disambiguationData":[TD([[subQ4,1.0]])],"derivedFrom":subQ3}),1.0]])]});}
            var Q43;
            {var subQ0=sQuery(id+"F0.wireOp",EDGE,"E108.MirrorCS");var subQ3=sQuery(id+"F0.wireOp",EDGE,"E3");var subQ4=makeQuery(id+"F0.imprint","INTERSECT",VERTEX,{"derivedFrom":[subQ3,subQ0]});Q43=makeQuery(id+"F0.imprint","IMPRINT",FACE,{"disambiguationData":[TD([[makeQuery(id+"F0.imprint","IMPRINT",EDGE,{"disambiguationData":[TD([[subQ4,-1.0]])],"derivedFrom":subQ3}),1.0]])]});}
            var Q44;
            {var subQ0=sQuery(id+"F0.wireOp",EDGE,"E90.MirrorCS");var subQ3=sQuery(id+"F0.wireOp",EDGE,"E3");var subQ4=makeQuery(id+"F0.imprint","INTERSECT",VERTEX,{"derivedFrom":[subQ3,subQ0]});Q44=makeQuery(id+"F0.imprint","IMPRINT",FACE,{"disambiguationData":[TD([[makeQuery(id+"F0.imprint","IMPRINT",EDGE,{"disambiguationData":[TD([[subQ4,-1.0]])],"derivedFrom":subQ3}),1.0]])]});}
            var Q45;
            {var subQ3=sQuery(id+"F0.wireOp",EDGE,"E3");var subQ5=sQuery(id+"F0.wireOp",EDGE,"E110.MirrorCS");var subQ7=makeQuery(id+"F0.imprint","INTERSECT",VERTEX,{"derivedFrom":[subQ3,subQ5]});Q45=makeQuery(id+"F0.imprint","IMPRINT",FACE,{"disambiguationData":[TD([[makeQuery(id+"F0.imprint","IMPRINT",EDGE,{"disambiguationData":[TD([[subQ7,-1.0]])],"derivedFrom":subQ3}),1.0]])]});}
            var Q46;
            {var subQ0=sQuery(id+"F0.wireOp",EDGE,"E81.MirrorCS");var subQ3=sQuery(id+"F0.wireOp",EDGE,"E3");var subQ4=makeQuery(id+"F0.imprint","INTERSECT",VERTEX,{"derivedFrom":[subQ3,subQ0]});Q46=makeQuery(id+"F0.imprint","IMPRINT",FACE,{"disambiguationData":[TD([[makeQuery(id+"F0.imprint","IMPRINT",EDGE,{"disambiguationData":[TD([[subQ4,-1.0]])],"derivedFrom":subQ3}),1.0]])]});}
            var Q47;
            {var subQ3=sQuery(id+"F0.wireOp",EDGE,"E79.MirrorCS");var subQ5=sQuery(id+"F0.wireOp",EDGE,"E3");var subQ7=makeQuery(id+"F0.imprint","INTERSECT",VERTEX,{"derivedFrom":[subQ5,subQ3]});Q47=makeQuery(id+"F0.imprint","IMPRINT",FACE,{"disambiguationData":[TD([[makeQuery(id+"F0.imprint","IMPRINT",EDGE,{"disambiguationData":[TD([[subQ7,-1.0]])],"derivedFrom":subQ5}),1.0]])]});}
            var Q48;
            {var subQ0=sQuery(id+"F0.wireOp",EDGE,"E80.MirrorCS");var subQ3=sQuery(id+"F0.wireOp",EDGE,"E3");var subQ4=makeQuery(id+"F0.imprint","INTERSECT",VERTEX,{"derivedFrom":[subQ3,subQ0]});Q48=makeQuery(id+"F0.imprint","IMPRINT",FACE,{"disambiguationData":[TD([[makeQuery(id+"F0.imprint","IMPRINT",EDGE,{"disambiguationData":[TD([[subQ4,-1.0]])],"derivedFrom":subQ3}),1.0]])]});}
            var Q49;
            {var subQ0=sQuery(id+"F0.wireOp",EDGE,"E107.MirrorCS");var subQ3=sQuery(id+"F0.wireOp",EDGE,"E3");var subQ4=makeQuery(id+"F0.imprint","INTERSECT",VERTEX,{"derivedFrom":[subQ3,subQ0]});Q49=makeQuery(id+"F0.imprint","IMPRINT",FACE,{"disambiguationData":[TD([[makeQuery(id+"F0.imprint","IMPRINT",EDGE,{"disambiguationData":[TD([[subQ4,-1.0]])],"derivedFrom":subQ3}),1.0]])]});}
            var Q50;
            {var subQ3=sQuery(id+"F0.wireOp",EDGE,"E3");var subQ5=sQuery(id+"F0.wireOp",EDGE,"E106.MirrorCS");var subQ7=makeQuery(id+"F0.imprint","INTERSECT",VERTEX,{"derivedFrom":[subQ3,subQ5]});Q50=makeQuery(id+"F0.imprint","IMPRINT",FACE,{"disambiguationData":[TD([[makeQuery(id+"F0.imprint","IMPRINT",EDGE,{"disambiguationData":[TD([[subQ7,-1.0]])],"derivedFrom":subQ3}),1.0]])]});}
            var Q51;
            {var subQ3=sQuery(id+"F0.wireOp",EDGE,"E3");var subQ5=sQuery(id+"F0.wireOp",EDGE,"E92.MirrorCS");var subQ7=makeQuery(id+"F0.imprint","INTERSECT",VERTEX,{"derivedFrom":[subQ3,subQ5]});Q51=makeQuery(id+"F0.imprint","IMPRINT",FACE,{"disambiguationData":[TD([[makeQuery(id+"F0.imprint","IMPRINT",EDGE,{"disambiguationData":[TD([[subQ7,-1.0]])],"derivedFrom":subQ3}),1.0]])]});}
            var Q52;
            {var subQ3=sQuery(id+"F0.wireOp",EDGE,"E3");var subQ5=sQuery(id+"F0.wireOp",EDGE,"E7.0.left");var subQ7=makeQuery(id+"F0.imprint","INTERSECT",VERTEX,{"derivedFrom":[subQ3,subQ5]});Q52=makeQuery(id+"F0.imprint","IMPRINT",FACE,{"disambiguationData":[TD([[makeQuery(id+"F0.imprint","IMPRINT",EDGE,{"disambiguationData":[TD([[subQ7,-1.0]])],"derivedFrom":subQ3}),1.0]])]});}
            var Q53;
            {var subQ1=sQuery(id+"F0.wireOp",EDGE,"E6");var subQ5=sQuery(id+"F0.wireOp",EDGE,"E3");var subQ6=makeQuery(id+"F0.imprint","INTERSECT",VERTEX,{"derivedFrom":[subQ5,subQ1]});Q53=makeQuery(id+"F0.imprint","IMPRINT",FACE,{"disambiguationData":[TD([[makeQuery(id+"F0.imprint","IMPRINT",EDGE,{"disambiguationData":[TD([[subQ6,-1.0]])],"derivedFrom":subQ5}),1.0]])]});}
            var Q54;
            {var subQ3=sQuery(id+"F0.wireOp",EDGE,"E7.0.right");var subQ5=sQuery(id+"F0.wireOp",EDGE,"E3");var subQ7=makeQuery(id+"F0.imprint","INTERSECT",VERTEX,{"derivedFrom":[subQ5,subQ3]});Q54=makeQuery(id+"F0.imprint","IMPRINT",FACE,{"disambiguationData":[TD([[makeQuery(id+"F0.imprint","IMPRINT",EDGE,{"disambiguationData":[TD([[subQ7,-1.0]])],"derivedFrom":subQ5}),1.0]])]});}
            var Q55;
            {var subQ3=sQuery(id+"F0.wireOp",EDGE,"E13.0.left");var subQ5=sQuery(id+"F0.wireOp",EDGE,"E3");var subQ7=makeQuery(id+"F0.imprint","INTERSECT",VERTEX,{"derivedFrom":[subQ5,subQ3]});Q55=makeQuery(id+"F0.imprint","IMPRINT",FACE,{"disambiguationData":[TD([[makeQuery(id+"F0.imprint","IMPRINT",EDGE,{"disambiguationData":[TD([[subQ7,-1.0]])],"derivedFrom":subQ5}),1.0]])]});}
            var Q56;
            {var subQ3=sQuery(id+"F0.wireOp",EDGE,"E3");var subQ5=sQuery(id+"F0.wireOp",EDGE,"E12");var subQ7=makeQuery(id+"F0.imprint","INTERSECT",VERTEX,{"derivedFrom":[subQ3,subQ5]});Q56=makeQuery(id+"F0.imprint","IMPRINT",FACE,{"disambiguationData":[TD([[makeQuery(id+"F0.imprint","IMPRINT",EDGE,{"disambiguationData":[TD([[subQ7,-1.0]])],"derivedFrom":subQ3}),1.0]])]});}
            var Q57;
            {var subQ0=sQuery(id+"F0.wireOp",EDGE,"E13.0.right");var subQ3=sQuery(id+"F0.wireOp",EDGE,"E3");var subQ4=makeQuery(id+"F0.imprint","INTERSECT",VERTEX,{"derivedFrom":[subQ3,subQ0]});Q57=makeQuery(id+"F0.imprint","IMPRINT",FACE,{"disambiguationData":[TD([[makeQuery(id+"F0.imprint","IMPRINT",EDGE,{"disambiguationData":[TD([[subQ4,-1.0]])],"derivedFrom":subQ3}),1.0]])]});}
            var Q58;
            {var subQ1=sQuery(id+"F0.wireOp",EDGE,"E9.0.left");var subQ5=sQuery(id+"F0.wireOp",EDGE,"E3");var subQ7=makeQuery(id+"F0.imprint","INTERSECT",VERTEX,{"derivedFrom":[subQ5,subQ1]});Q58=makeQuery(id+"F0.imprint","IMPRINT",FACE,{"disambiguationData":[TD([[makeQuery(id+"F0.imprint","IMPRINT",EDGE,{"disambiguationData":[TD([[subQ7,-1.0]])],"derivedFrom":subQ5}),1.0]])]});}
            var Q59;
            {var subQ1=sQuery(id+"F0.wireOp",EDGE,"E9.0.left");var subQ5=sQuery(id+"F0.wireOp",EDGE,"E3");var subQ7=makeQuery(id+"F0.imprint","INTERSECT",VERTEX,{"derivedFrom":[subQ5,subQ1]});Q59=makeQuery(id+"F0.imprint","IMPRINT",FACE,{"disambiguationData":[TD([[makeQuery(id+"F0.imprint","IMPRINT",EDGE,{"disambiguationData":[TD([[subQ7,1.0]])],"derivedFrom":subQ5}),1.0]])]});}
            var Q60;
            {var subQ3=sQuery(id+"F0.wireOp",EDGE,"E8");var subQ5=sQuery(id+"F0.wireOp",EDGE,"E3");var subQ7=makeQuery(id+"F0.imprint","INTERSECT",VERTEX,{"derivedFrom":[subQ5,subQ3]});Q60=makeQuery(id+"F0.imprint","IMPRINT",FACE,{"disambiguationData":[TD([[makeQuery(id+"F0.imprint","IMPRINT",EDGE,{"disambiguationData":[TD([[subQ7,1.0]])],"derivedFrom":subQ5}),1.0]])]});}
            var Q61;
            {var subQ3=sQuery(id+"F0.wireOp",EDGE,"E3");var subQ5=sQuery(id+"F0.wireOp",EDGE,"E44.MirrorCS");var subQ7=makeQuery(id+"F0.imprint","INTERSECT",VERTEX,{"derivedFrom":[subQ3,subQ5]});Q61=makeQuery(id+"F0.imprint","IMPRINT",FACE,{"disambiguationData":[TD([[makeQuery(id+"F0.imprint","IMPRINT",EDGE,{"disambiguationData":[TD([[subQ7,-1.0]])],"derivedFrom":subQ3}),1.0]])]});}
            var Q62;
            {var subQ3=sQuery(id+"F0.wireOp",EDGE,"E39.MirrorCS");var subQ5=sQuery(id+"F0.wireOp",EDGE,"E3");var subQ7=makeQuery(id+"F0.imprint","INTERSECT",VERTEX,{"derivedFrom":[subQ5,subQ3]});Q62=makeQuery(id+"F0.imprint","IMPRINT",FACE,{"disambiguationData":[TD([[makeQuery(id+"F0.imprint","IMPRINT",EDGE,{"disambiguationData":[TD([[subQ7,-1.0]])],"derivedFrom":subQ5}),1.0]])]});}
            var Q63;
            {var subQ1=sQuery(id+"F0.wireOp",EDGE,"E50.MirrorCS");var subQ5=sQuery(id+"F0.wireOp",EDGE,"E3");var subQ6=makeQuery(id+"F0.imprint","INTERSECT",VERTEX,{"derivedFrom":[subQ5,subQ1]});Q63=makeQuery(id+"F0.imprint","IMPRINT",FACE,{"disambiguationData":[TD([[makeQuery(id+"F0.imprint","IMPRINT",EDGE,{"disambiguationData":[TD([[subQ6,-1.0]])],"derivedFrom":subQ5}),1.0]])]});}
            var Q64;
            {var subQ1=sQuery(id+"F0.wireOp",EDGE,"E43.MirrorCS");var subQ5=sQuery(id+"F0.wireOp",EDGE,"E3");var subQ6=makeQuery(id+"F0.imprint","INTERSECT",VERTEX,{"derivedFrom":[subQ5,subQ1]});Q64=makeQuery(id+"F0.imprint","IMPRINT",FACE,{"disambiguationData":[TD([[makeQuery(id+"F0.imprint","IMPRINT",EDGE,{"disambiguationData":[TD([[subQ6,-1.0]])],"derivedFrom":subQ5}),1.0]])]});}
            var Q65;
            {var subQ0=sQuery(id+"F0.wireOp",EDGE,"E41.MirrorCS");var subQ3=sQuery(id+"F0.wireOp",EDGE,"E3");var subQ4=makeQuery(id+"F0.imprint","INTERSECT",VERTEX,{"derivedFrom":[subQ3,subQ0]});Q65=makeQuery(id+"F0.imprint","IMPRINT",FACE,{"disambiguationData":[TD([[makeQuery(id+"F0.imprint","IMPRINT",EDGE,{"disambiguationData":[TD([[subQ4,-1.0]])],"derivedFrom":subQ3}),1.0]])]});}
            var Q66;
            {var subQ3=sQuery(id+"F0.wireOp",EDGE,"E3");var subQ5=sQuery(id+"F0.wireOp",EDGE,"E42.MirrorCS");var subQ7=makeQuery(id+"F0.imprint","INTERSECT",VERTEX,{"derivedFrom":[subQ3,subQ5]});Q66=makeQuery(id+"F0.imprint","IMPRINT",FACE,{"disambiguationData":[TD([[makeQuery(id+"F0.imprint","IMPRINT",EDGE,{"disambiguationData":[TD([[subQ7,-1.0]])],"derivedFrom":subQ3}),1.0]])]});}
            var Q67;
            {var subQ1=sQuery(id+"F0.wireOp",EDGE,"E87.MirrorCS");var subQ5=sQuery(id+"F0.wireOp",EDGE,"E64.MirrorCS");var subQ6=makeQuery(id+"F0.imprint","INTERSECT",VERTEX,{"derivedFrom":[subQ5,subQ1]});Q67=makeQuery(id+"F0.imprint","IMPRINT",FACE,{"disambiguationData":[TD([[makeQuery(id+"F0.imprint","IMPRINT",EDGE,{"disambiguationData":[TD([[subQ6,-1.0]])],"derivedFrom":subQ5}),1.0]])]});}
            var Q68;
            {var subQ1=sQuery(id+"F0.wireOp",EDGE,"E87.MirrorCS");var subQ5=sQuery(id+"F0.wireOp",EDGE,"E64.MirrorCS");var subQ7=makeQuery(id+"F0.imprint","INTERSECT",VERTEX,{"derivedFrom":[subQ5,subQ1]});Q68=makeQuery(id+"F0.imprint","IMPRINT",FACE,{"disambiguationData":[TD([[makeQuery(id+"F0.imprint","IMPRINT",EDGE,{"disambiguationData":[TD([[subQ7,-1.0]])],"derivedFrom":subQ5}),-1.0]])]});}
            var Q69;
            {var subQ0=sQuery(id+"F0.wireOp",EDGE,"E99.MirrorCS");var subQ1=sQuery(id+"F0.wireOp",EDGE,"E87.MirrorCS");var subQ2=makeQuery(id+"F0.imprint","INTERSECT",VERTEX,{"derivedFrom":[subQ1,subQ0]});Q69=makeQuery(id+"F0.imprint","IMPRINT",FACE,{"disambiguationData":[TD([[makeQuery(id+"F0.imprint","IMPRINT",EDGE,{"disambiguationData":[TD([[subQ2,-1.0]])],"derivedFrom":subQ1}),1.0]])]});}
            var Q70;
            {var subQ0=sQuery(id+"F0.wireOp",EDGE,"E86.MirrorCS");var subQ3=sQuery(id+"F0.wireOp",EDGE,"E95.MirrorCS");var subQ4=makeQuery(id+"F0.imprint","INTERSECT",VERTEX,{"derivedFrom":[subQ0,subQ3]});Q70=makeQuery(id+"F0.imprint","IMPRINT",FACE,{"disambiguationData":[TD([[makeQuery(id+"F0.imprint","IMPRINT",EDGE,{"disambiguationData":[TD([[subQ4,-1.0]])],"derivedFrom":subQ0}),-1.0]])]});}
            var Q71;
            {var subQ1=sQuery(id+"F0.wireOp",EDGE,"E86.MirrorCS");var subQ5=sQuery(id+"F0.wireOp",EDGE,"E65.MirrorCS");var subQ6=makeQuery(id+"F0.imprint","INTERSECT",VERTEX,{"derivedFrom":[subQ5,subQ1]});Q71=makeQuery(id+"F0.imprint","IMPRINT",FACE,{"disambiguationData":[TD([[makeQuery(id+"F0.imprint","IMPRINT",EDGE,{"disambiguationData":[TD([[subQ6,-1.0]])],"derivedFrom":subQ5}),1.0]])]});}
            var Q72;
            {var subQ0=sQuery(id+"F0.wireOp",EDGE,"E86.MirrorCS");var subQ3=sQuery(id+"F0.wireOp",EDGE,"E65.MirrorCS");var subQ4=makeQuery(id+"F0.imprint","INTERSECT",VERTEX,{"derivedFrom":[subQ3,subQ0]});Q72=makeQuery(id+"F0.imprint","IMPRINT",FACE,{"disambiguationData":[TD([[makeQuery(id+"F0.imprint","IMPRINT",EDGE,{"disambiguationData":[TD([[subQ4,-1.0]])],"derivedFrom":subQ3}),-1.0]])]});}
            var Q73;
            {var subQ0=sQuery(id+"F0.wireOp",EDGE,"E80.MirrorCS");var subQ3=sQuery(id+"F0.wireOp",EDGE,"E3");var subQ4=makeQuery(id+"F0.imprint","INTERSECT",VERTEX,{"derivedFrom":[subQ3,subQ0]});Q73=makeQuery(id+"F0.imprint","IMPRINT",FACE,{"disambiguationData":[TD([[makeQuery(id+"F0.imprint","IMPRINT",EDGE,{"disambiguationData":[TD([[subQ4,-1.0]])],"derivedFrom":subQ3}),-1.0]])]});}
            var Q74;
            {var subQ0=sQuery(id+"F0.wireOp",EDGE,"E79.MirrorCS");var subQ3=sQuery(id+"F0.wireOp",EDGE,"E3");var subQ4=makeQuery(id+"F0.imprint","INTERSECT",VERTEX,{"derivedFrom":[subQ3,subQ0]});Q74=makeQuery(id+"F0.imprint","IMPRINT",FACE,{"disambiguationData":[TD([[makeQuery(id+"F0.imprint","IMPRINT",EDGE,{"disambiguationData":[TD([[subQ4,-1.0]])],"derivedFrom":subQ3}),-1.0]])]});}
            var Q75;
            {var subQ3=sQuery(id+"F0.wireOp",EDGE,"E3");var subQ5=sQuery(id+"F0.wireOp",EDGE,"E106.MirrorCS");var subQ7=makeQuery(id+"F0.imprint","INTERSECT",VERTEX,{"derivedFrom":[subQ3,subQ5]});Q75=makeQuery(id+"F0.imprint","IMPRINT",FACE,{"disambiguationData":[TD([[makeQuery(id+"F0.imprint","IMPRINT",EDGE,{"disambiguationData":[TD([[subQ7,-1.0]])],"derivedFrom":subQ3}),-1.0]])]});}
            var Q76;
            {var subQ3=sQuery(id+"F0.wireOp",EDGE,"E3");var subQ5=sQuery(id+"F0.wireOp",EDGE,"E92.MirrorCS");var subQ7=makeQuery(id+"F0.imprint","INTERSECT",VERTEX,{"derivedFrom":[subQ3,subQ5]});Q76=makeQuery(id+"F0.imprint","IMPRINT",FACE,{"disambiguationData":[TD([[makeQuery(id+"F0.imprint","IMPRINT",EDGE,{"disambiguationData":[TD([[subQ7,-1.0]])],"derivedFrom":subQ3}),-1.0]])]});}
            var Q77;
            {var subQ3=sQuery(id+"F0.wireOp",EDGE,"E3");var subQ5=sQuery(id+"F0.wireOp",EDGE,"E6");var subQ7=makeQuery(id+"F0.imprint","INTERSECT",VERTEX,{"derivedFrom":[subQ3,subQ5]});Q77=makeQuery(id+"F0.imprint","IMPRINT",FACE,{"disambiguationData":[TD([[makeQuery(id+"F0.imprint","IMPRINT",EDGE,{"disambiguationData":[TD([[subQ7,-1.0]])],"derivedFrom":subQ3}),-1.0]])]});}
            var Q78;
            {var subQ0=sQuery(id+"F0.wireOp",EDGE,"E7.0.right");var subQ3=sQuery(id+"F0.wireOp",EDGE,"E3");var subQ4=makeQuery(id+"F0.imprint","INTERSECT",VERTEX,{"derivedFrom":[subQ3,subQ0]});Q78=makeQuery(id+"F0.imprint","IMPRINT",FACE,{"disambiguationData":[TD([[makeQuery(id+"F0.imprint","IMPRINT",EDGE,{"disambiguationData":[TD([[subQ4,-1.0]])],"derivedFrom":subQ3}),-1.0]])]});}
            var Q79;
            {var subQ0=sQuery(id+"F0.wireOp",EDGE,"E12");var subQ3=sQuery(id+"F0.wireOp",EDGE,"E3");var subQ4=makeQuery(id+"F0.imprint","INTERSECT",VERTEX,{"derivedFrom":[subQ3,subQ0]});Q79=makeQuery(id+"F0.imprint","IMPRINT",FACE,{"disambiguationData":[TD([[makeQuery(id+"F0.imprint","IMPRINT",EDGE,{"disambiguationData":[TD([[subQ4,-1.0]])],"derivedFrom":subQ3}),-1.0]])]});}
            var Q80;
            {var subQ3=sQuery(id+"F0.wireOp",EDGE,"E3");var subQ5=sQuery(id+"F0.wireOp",EDGE,"E13.0.right");var subQ7=makeQuery(id+"F0.imprint","INTERSECT",VERTEX,{"derivedFrom":[subQ3,subQ5]});Q80=makeQuery(id+"F0.imprint","IMPRINT",FACE,{"disambiguationData":[TD([[makeQuery(id+"F0.imprint","IMPRINT",EDGE,{"disambiguationData":[TD([[subQ7,-1.0]])],"derivedFrom":subQ3}),-1.0]])]});}
            var Q81;
            {var subQ3=sQuery(id+"F0.wireOp",EDGE,"E3");var subQ5=sQuery(id+"F0.wireOp",EDGE,"E9.0.left");var subQ7=makeQuery(id+"F0.imprint","INTERSECT",VERTEX,{"derivedFrom":[subQ3,subQ5]});Q81=makeQuery(id+"F0.imprint","IMPRINT",FACE,{"disambiguationData":[TD([[makeQuery(id+"F0.imprint","IMPRINT",EDGE,{"disambiguationData":[TD([[subQ7,1.0]])],"derivedFrom":subQ3}),-1.0]])]});}
            var Q82;
            {var subQ0=sQuery(id+"F0.wireOp",EDGE,"E8");var subQ3=sQuery(id+"F0.wireOp",EDGE,"E3");var subQ4=makeQuery(id+"F0.imprint","INTERSECT",VERTEX,{"derivedFrom":[subQ3,subQ0]});Q82=makeQuery(id+"F0.imprint","IMPRINT",FACE,{"disambiguationData":[TD([[makeQuery(id+"F0.imprint","IMPRINT",EDGE,{"disambiguationData":[TD([[subQ4,1.0]])],"derivedFrom":subQ3}),-1.0]])]});}
            var Q83;
            {var subQ3=sQuery(id+"F0.wireOp",EDGE,"E3");var subQ5=sQuery(id+"F0.wireOp",EDGE,"E39.MirrorCS");var subQ7=makeQuery(id+"F0.imprint","INTERSECT",VERTEX,{"derivedFrom":[subQ3,subQ5]});Q83=makeQuery(id+"F0.imprint","IMPRINT",FACE,{"disambiguationData":[TD([[makeQuery(id+"F0.imprint","IMPRINT",EDGE,{"disambiguationData":[TD([[subQ7,-1.0]])],"derivedFrom":subQ3}),-1.0]])]});}
            var Q84;
            {var subQ0=sQuery(id+"F0.wireOp",EDGE,"E50.MirrorCS");var subQ3=sQuery(id+"F0.wireOp",EDGE,"E3");var subQ4=makeQuery(id+"F0.imprint","INTERSECT",VERTEX,{"derivedFrom":[subQ3,subQ0]});Q84=makeQuery(id+"F0.imprint","IMPRINT",FACE,{"disambiguationData":[TD([[makeQuery(id+"F0.imprint","IMPRINT",EDGE,{"disambiguationData":[TD([[subQ4,-1.0]])],"derivedFrom":subQ3}),-1.0]])]});}
            var Q85;
            {var subQ0=sQuery(id+"F0.wireOp",EDGE,"E41.MirrorCS");var subQ3=sQuery(id+"F0.wireOp",EDGE,"E3");var subQ4=makeQuery(id+"F0.imprint","INTERSECT",VERTEX,{"derivedFrom":[subQ3,subQ0]});Q85=makeQuery(id+"F0.imprint","IMPRINT",FACE,{"disambiguationData":[TD([[makeQuery(id+"F0.imprint","IMPRINT",EDGE,{"disambiguationData":[TD([[subQ4,-1.0]])],"derivedFrom":subQ3}),-1.0]])]});}
            var Q86;
            {var subQ3=sQuery(id+"F0.wireOp",EDGE,"E3");var subQ5=sQuery(id+"F0.wireOp",EDGE,"E42.MirrorCS");var subQ7=makeQuery(id+"F0.imprint","INTERSECT",VERTEX,{"derivedFrom":[subQ3,subQ5]});Q86=makeQuery(id+"F0.imprint","IMPRINT",FACE,{"disambiguationData":[TD([[makeQuery(id+"F0.imprint","IMPRINT",EDGE,{"disambiguationData":[TD([[subQ7,-1.0]])],"derivedFrom":subQ3}),-1.0]])]});}
            var Q87;
            {var subQ0=sQuery(id+"F0.wireOp",EDGE,"E90.MirrorCS");var subQ3=sQuery(id+"F0.wireOp",EDGE,"E3");var subQ4=makeQuery(id+"F0.imprint","INTERSECT",VERTEX,{"derivedFrom":[subQ3,subQ0]});Q87=makeQuery(id+"F0.imprint","IMPRINT",FACE,{"disambiguationData":[TD([[makeQuery(id+"F0.imprint","IMPRINT",EDGE,{"disambiguationData":[TD([[subQ4,-1.0]])],"derivedFrom":subQ3}),-1.0]])]});}
            var Q88;
            {var subQ0=sQuery(id+"F0.wireOp",EDGE,"E110.MirrorCS");var subQ3=sQuery(id+"F0.wireOp",EDGE,"E3");var subQ4=makeQuery(id+"F0.imprint","INTERSECT",VERTEX,{"derivedFrom":[subQ3,subQ0]});Q88=makeQuery(id+"F0.imprint","IMPRINT",FACE,{"disambiguationData":[TD([[makeQuery(id+"F0.imprint","IMPRINT",EDGE,{"disambiguationData":[TD([[subQ4,-1.0]])],"derivedFrom":subQ3}),-1.0]])]});}
            extrude(context, id + "F1", {"entities" : qUnion([Q0, Q1, Q2, Q3, Q4, Q5, Q6, Q7, Q8, Q9, Q10, Q11, Q12, Q13, Q14, Q15, Q16, Q17, Q18, Q19, Q20, Q21, Q22, Q23, Q24, Q25, Q26, Q27, Q28, Q29, Q30, Q31, Q32, Q33, Q34, Q35, Q36, Q37, Q38, Q39, Q40, Q41, Q42, Q43, Q44, Q45, Q46, Q47, Q48, Q49, Q50, Q51, Q52, Q53, Q54, Q55, Q56, Q57, Q58, Q59, Q60, Q61, Q62, Q63, Q64, Q65, Q66, Q67, Q68, Q69, Q70, Q71, Q72, Q73, Q74, Q75, Q76, Q77, Q78, Q79, Q80, Q81, Q82, Q83, Q84, Q85, Q86, Q87, Q88]), "depth" : 2 * mm});
        }
    });
